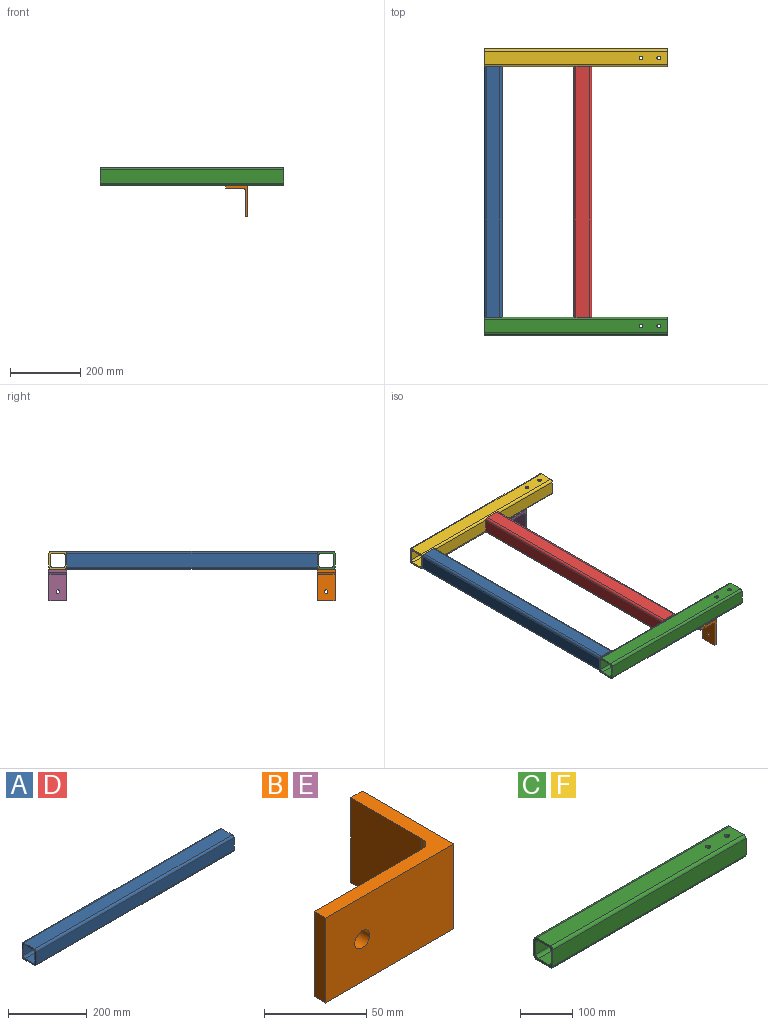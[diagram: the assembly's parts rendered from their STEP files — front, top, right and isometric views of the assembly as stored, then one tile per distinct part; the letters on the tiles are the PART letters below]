
ASSEMBLY  parts=6 mates=5
PART A: 18 faces, bbox 711.2x50.8x50.8 mm
  f0: cylinder r=6.35mm len=711.2mm, axis (-1,0,0), area 7093.9mm2, adj f1,f15,f16,f17
  f1: plane 711.2x38.1mm, normal (0,0,-1), area 27096.7mm2, adj f0,f2,f16,f17
  f2: cylinder r=6.35mm len=711.2mm, axis (-1,0,0), area 7093.9mm2, adj f1,f3,f16,f17
  f3: plane 711.2x38.1mm, normal (0,1,0), area 27096.7mm2, adj f2,f4,f16,f17
  f4: cylinder r=6.35mm len=711.2mm, axis (-1,0,0), area 7093.9mm2, adj f3,f5,f16,f17
  f5: plane 711.2x38.1mm, normal (0,0,1), area 27096.7mm2, adj f4,f6,f16,f17
  f6: cylinder r=6.35mm len=711.2mm, axis (-1,0,0), area 7093.9mm2, adj f5,f15,f16,f17
  f7: plane 711.2x28.58mm, normal (0,0,1), area 20322.5mm2, adj f8,f14,f16,f17
  f8: cylinder r=6.35mm len=711.2mm, axis (-1,0,0), area 7093.9mm2, adj f7,f9,f16,f17
  f9: plane 711.2x28.58mm, normal (0,1,0), area 20322.5mm2, adj f8,f10,f16,f17
  f10: cylinder r=6.35mm len=711.2mm, axis (-1,0,0), area 7093.9mm2, adj f9,f11,f16,f17
  f11: plane 711.2x28.58mm, normal (0,0,-1), area 20322.5mm2, adj f10,f12,f16,f17
  f12: cylinder r=6.35mm len=711.2mm, axis (-1,0,0), area 7093.9mm2, adj f11,f13,f16,f17
  f13: plane 711.2x28.58mm, normal (0,-1,0), area 20322.5mm2, adj f12,f14,f16,f17
  f14: cylinder r=6.35mm len=711.2mm, axis (-1,0,0), area 7093.9mm2, adj f7,f13,f16,f17
  f15: plane 711.2x38.1mm, normal (0,-1,0), area 27096.7mm2, adj f0,f6,f16,f17
  f16: plane 50.8x50.8mm, normal (1,0,0), area 877mm2, adj f0,f1,f2,f3,f4,f5,f6,f7
  f17: plane 50.8x50.8mm, normal (-1,0,0), area 877mm2, adj f0,f1,f2,f3,f4,f5,f6,f7
PART B: 10 faces, bbox 88.9x63.5x50.8 mm
  f0: plane 88.9x50.8mm, normal (0,-1,0), area 4433.4mm2, adj f1,f6,f7,f8,f9
  f1: plane 63.5x50.8mm, normal (1,0,0), area 3225.8mm2, adj f0,f2,f7,f8
  f2: plane 50.8x7.94mm, normal (0,1,0), area 403.2mm2, adj f1,f3,f7,f8
  f3: plane 50.8x49.21mm, normal (-1,0,0), area 2500mm2, adj f2,f4,f7,f8
  f4: cylinder r=6.35mm len=50.8mm, axis (0,0,-1), area 506.7mm2, adj f3,f5,f7,f8
  f5: plane 74.61x50.8mm, normal (0,1,0), area 3707.6mm2, adj f4,f6,f7,f8,f9
  f6: plane 50.8x7.94mm, normal (-1,0,0), area 403.2mm2, adj f0,f5,f7,f8
  f7: plane 88.9x63.5mm, normal (0,0,1), area 1155.3mm2, adj f0,f1,f2,f3,f4,f5,f6
  f8: plane 88.9x63.5mm, normal (0,0,-1), area 1155.3mm2, adj f0,f1,f2,f3,f4,f5,f6
  f9: cylinder r=5.13mm len=10.26mm, axis (0,-1,0), area 255.9mm2, adj f0,f5
PART C: 22 faces, bbox 520.7x50.8x50.8 mm
  f0: cylinder r=6.35mm len=520.7mm, axis (-1,0,0), area 5193.8mm2, adj f1,f15,f16,f17
  f1: plane 520.7x38.1mm, normal (0,0,-1), area 19673.3mm2, adj f0,f2,f16,f17,f19,f21
  f2: cylinder r=6.35mm len=520.7mm, axis (-1,0,0), area 5193.8mm2, adj f1,f3,f16,f17
  f3: plane 520.7x38.1mm, normal (0,1,0), area 19838.7mm2, adj f2,f4,f16,f17
  f4: cylinder r=6.35mm len=520.7mm, axis (-1,0,0), area 5193.8mm2, adj f3,f5,f16,f17
  f5: plane 520.7x38.1mm, normal (0,0,1), area 19673.3mm2, adj f4,f6,f16,f17,f18,f20
  f6: cylinder r=6.35mm len=520.7mm, axis (-1,0,0), area 5193.8mm2, adj f5,f15,f16,f17
  f7: plane 520.7x28.58mm, normal (0,0,1), area 14713.6mm2, adj f8,f14,f16,f17,f19,f21
  f8: cylinder r=6.35mm len=520.7mm, axis (-1,0,0), area 5193.8mm2, adj f7,f9,f16,f17
  f9: plane 520.7x28.58mm, normal (0,1,0), area 14879mm2, adj f8,f10,f16,f17
  f10: cylinder r=6.35mm len=520.7mm, axis (-1,0,0), area 5193.8mm2, adj f9,f11,f16,f17
  f11: plane 520.7x28.58mm, normal (0,0,-1), area 14713.6mm2, adj f10,f12,f16,f17,f18,f20
  f12: cylinder r=6.35mm len=520.7mm, axis (-1,0,0), area 5193.8mm2, adj f11,f13,f16,f17
  f13: plane 520.7x28.58mm, normal (0,-1,0), area 14879mm2, adj f12,f14,f16,f17
  f14: cylinder r=6.35mm len=520.7mm, axis (-1,0,0), area 5193.8mm2, adj f7,f13,f16,f17
  f15: plane 520.7x38.1mm, normal (0,-1,0), area 19838.7mm2, adj f0,f6,f16,f17
  f16: plane 50.8x50.8mm, normal (1,0,0), area 877mm2, adj f0,f1,f2,f3,f4,f5,f6,f7
  f17: plane 50.8x50.8mm, normal (-1,0,0), area 877mm2, adj f0,f1,f2,f3,f4,f5,f6,f7
  f18: cylinder r=5.13mm len=10.26mm, axis (0,0,1), area 153.5mm2, adj f5,f11
  f19: cylinder r=5.13mm len=10.26mm, axis (0,0,1), area 153.5mm2, adj f1,f7
  f20: cylinder r=5.13mm len=10.26mm, axis (0,0,1), area 153.5mm2, adj f5,f11
  f21: cylinder r=5.13mm len=10.26mm, axis (0,0,1), area 153.5mm2, adj f1,f7
PART D: same geometry as A
PART E: same geometry as B
PART F: same geometry as C
PLACE A rot(axis=(0,0,-1),90deg) t=(33.06,121.83,-11.26)mm
PLACE B rot(axis=(0.58,-0.58,0.58),120deg) t=(395.01,-589.37,-40.63)mm
PLACE C t=(7.66,-614.77,-11.26)mm
PLACE D rot(axis=(0,0,-1),90deg) t=(287.06,121.83,-11.26)mm
PLACE E rot(axis=(0.58,-0.58,0.58),120deg) t=(395.01,172.63,-40.63)mm
PLACE F t=(7.66,147.23,-11.26)mm
MATE fastened E.f1 <-> F.f1  axis (0,0,1) through (426.76,147.23,-36.66)mm
MATE fastened A.f17 <-> F.f15  axis (0,1,0) through (7.66,121.83,-11.26)mm
MATE fastened B.f1 <-> C.f1  axis (0,0,1) through (426.76,-614.77,-36.66)mm
MATE fastened C.f3 <-> A.f16  axis (0,1,0) through (7.66,-589.37,-11.26)mm
MATE fastened D.f17 <-> F.f15  axis (0,1,0) through (312.46,121.83,-11.26)mm
